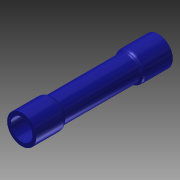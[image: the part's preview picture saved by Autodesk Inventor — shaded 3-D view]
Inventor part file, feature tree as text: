
AUTODESK INVENTOR PART (.ipt)
format: ipt  version: 2014 (Build 180170000, 170)  size: 170,496 bytes
history: native  units: in
note: dims shown in document units (in); Inventor stores cm internally (conversion verified against a paired STEP export)
features: sketch x3, extrude x2, fillet x2, projected_geometry x2, mirror x1, shell x1, revolve x1, chamfer x1
ambient origin geometry x8: Origin, YZ Plane, XZ Plane, XY Plane, X Axis, Y Axis, Z Axis, Center Point
bodies: Solid1 (feature_tree), Solid2 (feature_tree)
feature tree (13):
  extrude  "Extrusion1"  Depth=0.9735in TaperAngle=0.0deg
  extrude  "Extrusion2"  Depth=0.03in TaperAngle=0.0deg
  fillet  "Fillet1"  Radius=0.01in
  fillet  "Fillet2"  Radius=0.03in
  mirror  "Mirror1"
  shell  "Shell1"  Thickness=0.0265in
  revolve  "Revolution1"  [1 undecoded]
  chamfer  "Chamfer1"  Distance=0.03in
  sketch  "Sketch1"  dims[d0=0.175in d1=0.9735in d2=0.0in]
  sketch  "Sketch2"  dims[d3=0.207in d4=0.215in d5=0.0in d6=0.01in d7=0.03in d8=0.0265in]
  projected_geometry  "Projected Loop1"
  sketch  "Sketch3"  dims[d9=0.0145in d10=0.03in d11=0.03in d12=90.0deg d13=0.008in d14=0.125in d15=45.0deg]
  projected_geometry  "Project Cut Edges1"
note: 1 required parameter value undecoded (feature->parameter linkage not recoverable at this tier; creation-order binding heuristic only, values carry confidence <= 0.55)
